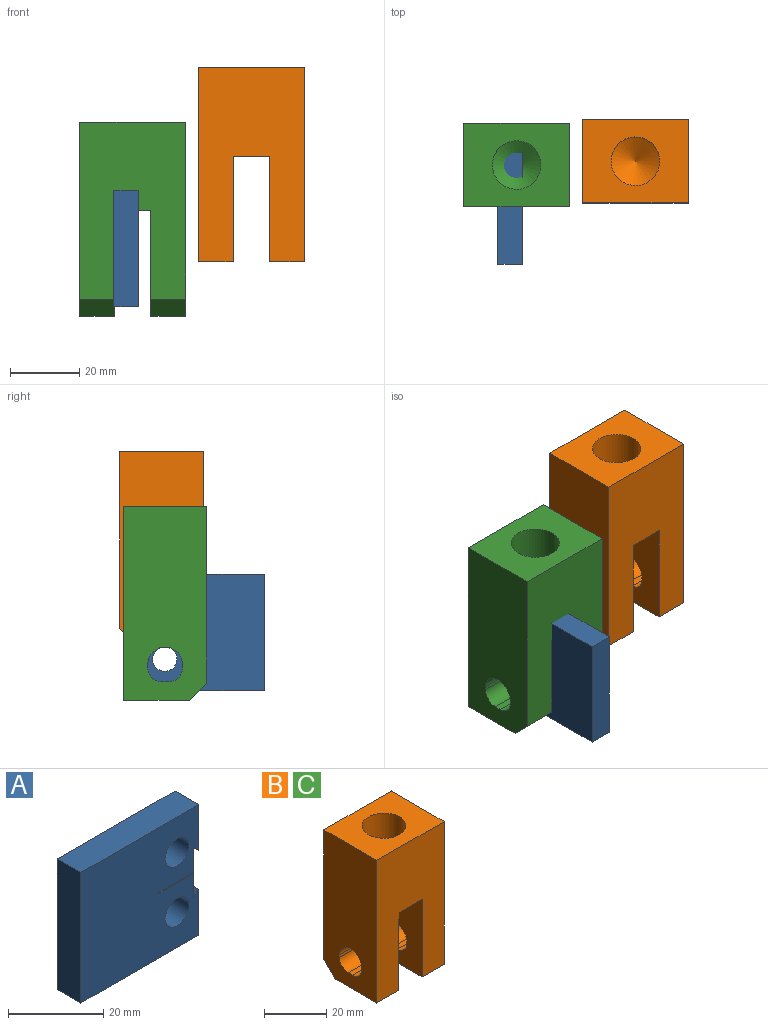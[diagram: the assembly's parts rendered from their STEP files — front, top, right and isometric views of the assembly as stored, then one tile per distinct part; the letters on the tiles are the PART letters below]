
ASSEMBLY  parts=3 mates=2
PART A: 16 faces, bbox 35x7x33.6 mm
  f0: plane 35x33.6mm, normal (0,-1,0), area 1079.1mm2, adj f2,f3,f4,f5,f6,f7,f8,f9
  f1: plane 35x33.6mm, normal (0,1,0), area 1079.1mm2, adj f2,f3,f4,f5,f6,f7,f8,f9
  f2: plane 11.8x7mm, normal (1,0,0), area 82.6mm2, adj f0,f1,f7,f14
  f3: plane 33.6x7mm, normal (-1,0,0), area 235.2mm2, adj f0,f1,f4,f7
  f4: plane 35x7mm, normal (0,0,-1), area 245mm2, adj f0,f1,f3,f5
  f5: plane 11.8x7mm, normal (1,0,0), area 82.6mm2, adj f0,f1,f4,f13
  f6: cylinder r=3.5mm len=7mm, axis (0,1,0), area 153.9mm2, adj f0,f1
  f7: plane 35x7mm, normal (0,0,1), area 245mm2, adj f0,f1,f2,f3
  f8: cylinder r=3.5mm len=7mm, axis (0,1,0), area 153.9mm2, adj f0,f1
  f9: plane 10.6x7mm, normal (0,0,-1), area 74.2mm2, adj f0,f1,f11,f15
  f10: plane 10.6x7mm, normal (0,0,1), area 74.2mm2, adj f0,f1,f11,f12
  f11: cylinder r=0.12mm len=7mm, axis (0,-1,0), area 2.7mm2, adj f0,f1,f9,f10
  f12: plane 7x6.38mm, normal (1,0,0), area 44.6mm2, adj f0,f1,f10,f13
  f13: plane 7x1.5mm, normal (-0.71,0,0.71), area 14.8mm2, adj f0,f1,f5,f12
  f14: plane 7x1.5mm, normal (-0.71,0,-0.71), area 14.8mm2, adj f0,f1,f2,f15
  f15: plane 7x6.38mm, normal (1,0,0), area 44.6mm2, adj f0,f1,f9,f14
PART B: 28 faces, bbox 30.5x24x56 mm
  f0: plane 56x24mm, normal (-1,0,0), area 1249.1mm2, adj f5,f6,f7,f8,f16,f17,f18,f19
  f1: plane 56x24mm, normal (1,0,0), area 1249.1mm2, adj f4,f5,f6,f7,f10,f11,f12,f13
  f2: plane 30.35x24mm, normal (1,0,0), area 633.5mm2, adj f5,f6,f8,f16,f17,f18,f19,f20
  f3: plane 30.35x24mm, normal (-1,0,0), area 633.5mm2, adj f4,f5,f6,f10,f11,f12,f13,f14
  f4: plane 19x10mm, normal (0,0,-1), area 190mm2, adj f1,f3,f5,f25
  f5: plane 56x30.5mm, normal (0,-1,0), area 1388.8mm2, adj f0,f1,f2,f3,f4,f7,f8,f9
  f6: plane 51x30.5mm, normal (0,1,0), area 1288.8mm2, adj f0,f1,f2,f3,f7,f9,f22,f23
  f7: plane 30.5x24mm, normal (0,0,1), area 578.1mm2, adj f0,f1,f5,f6,f27
  f8: plane 19x10mm, normal (0,0,-1), area 190mm2, adj f0,f2,f5,f24
  f9: plane 24x10.4mm, normal (0,0,-1), area 249.6mm2, adj f5,f6,f22,f23
  f10: plane 10x1mm, normal (0,-1,0), area 10mm2, adj f1,f3,f11,f15
  f11: cylinder r=4mm len=10mm, axis (1,0,0), area 62.8mm2, adj f1,f3,f10,f12
  f12: plane 10x2mm, normal (0,0,1), area 20mm2, adj f1,f3,f11,f13
  f13: cylinder r=4mm len=10mm, axis (1,0,0), area 62.8mm2, adj f1,f3,f12,f14
  f14: plane 10x1mm, normal (0,1,0), area 10mm2, adj f1,f3,f13,f15
  f15: cylinder r=5mm len=10mm, axis (1,0,0), area 157.1mm2, adj f1,f3,f10,f14
  f16: cylinder r=5mm len=10mm, axis (1,0,0), area 157.1mm2, adj f0,f2,f17,f21
  f17: plane 10x1mm, normal (0,1,0), area 10mm2, adj f0,f2,f16,f18
  f18: cylinder r=4mm len=10mm, axis (1,0,0), area 62.8mm2, adj f0,f2,f17,f19
  f19: plane 10x2mm, normal (0,0,1), area 20mm2, adj f0,f2,f18,f20
  f20: cylinder r=4mm len=10mm, axis (1,0,0), area 62.8mm2, adj f0,f2,f19,f21
  f21: plane 10x1mm, normal (0,-1,0), area 10mm2, adj f0,f2,f16,f20
  f22: cylinder r=0.05mm len=24mm, axis (0,-1,0), area 1.9mm2, adj f3,f5,f6,f9
  f23: cylinder r=0.05mm len=24mm, axis (0,1,0), area 1.9mm2, adj f2,f5,f6,f9
  f24: plane 10x5mm, normal (0,0.71,-0.71), area 70.7mm2, adj f0,f2,f6,f8
  f25: plane 10x5mm, normal (0,0.71,-0.71), area 70.7mm2, adj f1,f3,f4,f6
  f26: cone r=0mm half-angle=59deg, axis (0,0,1), area 179.6mm2, adj f27
  f27: cylinder r=7mm len=17.6mm, axis (0,0,1), area 774.1mm2, adj f7,f26
PART C: same geometry as B
PLACE A rot(axis=(0,0,1),90deg) t=(-10.01,-6.13,-141.53)mm
PLACE B t=(26.1,5.96,-117.38)mm
PLACE C rot(axis=(0,0,-1),180deg) t=(-8.12,4.9,-133.12)mm
MATE parallel A.f0 <-> B.f3  axis (1,0,0) through (-6.51,-7.21,-141.53)mm
MATE parallel C.f2 <-> A.f0  axis (-1,0,0) through (-2.87,5.9,-155.72)mm
